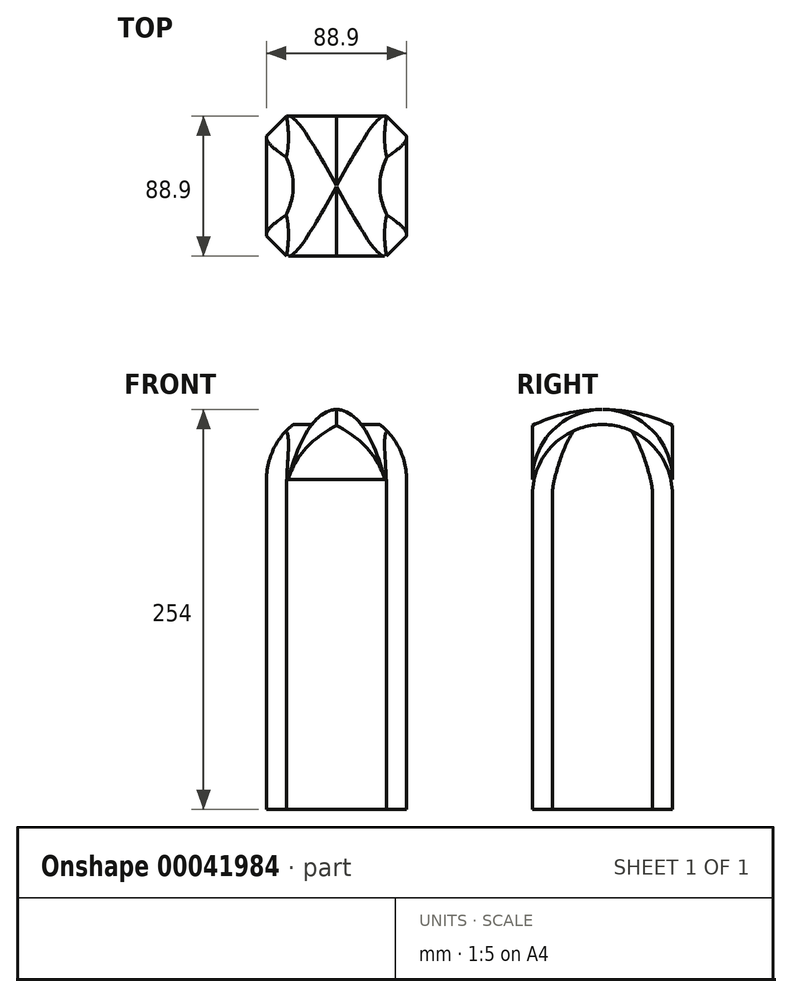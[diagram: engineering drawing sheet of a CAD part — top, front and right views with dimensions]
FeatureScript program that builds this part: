
annotation { "Feature Type Name" : "Feature", "Feature Type Description" : "" }
export const myFeature = defineFeature(function(context is Context, id is Id, definition is map)
    precondition{}
    {
        {
            var Q0;
            Q0=qCreatedBy(makeId("Top.planeOp"),FACE);
            var sketch = newSketch(context, id + "F0", { "sketchPlane" : qUnion([Q0])});
            skLineSegment(sketch, "E0.bottom", {"start": v(-44.45, 44.45) * mm, "end": v(44.45, 44.45) * mm});
            skLineSegment(sketch, "E0.top", {"start": v(-44.45, -44.45) * mm, "end": v(44.45, -44.45) * mm});
            skLineSegment(sketch, "E0.left", {"start": v(-44.45, 44.45) * mm, "end": v(-44.45, -44.45) * mm});
            skLineSegment(sketch, "E0.right", {"start": v(44.45, 44.45) * mm, "end": v(44.45, -44.45) * mm});
            skLineSegment(sketch, "E1", {"start": v(-44.45, 44.45) * mm, "end": v(44.45, -44.45) * mm});
            skLineSegment(sketch, "E2", {"start": v(44.45, 44.45) * mm, "end": v(-44.45, -44.45) * mm});
            skSolve(sketch);
        }
        {
            var Q0;
            Q0=qSketchRegion(id+"F0",true);
            extrude(context, id + "F1", {"entities" : qUnion([Q0]), "depth" : 152.4 * mm});
        }
        {
            var Q0;
            Q0=makeQuery(id+"F1.opExtrude","SWEPT_EDGE",EDGE,{"disambiguationData":[OSD([sQuery(id+"F0.wireOp",EDGE,"E0.top"),sQuery(id+"F0.wireOp",EDGE,"E0.right"),sQuery(id+"F0.wireOp",EDGE,"E1")])]});
            var Q1;
            Q1=makeQuery(id+"F1.opExtrude","SWEPT_EDGE",EDGE,{"disambiguationData":[OSD([sQuery(id+"F0.wireOp",EDGE,"E0.top"),sQuery(id+"F0.wireOp",EDGE,"E0.left"),sQuery(id+"F0.wireOp",EDGE,"E2")])]});
            var Q2;
            Q2=makeQuery(id+"F1.opExtrude","SWEPT_EDGE",EDGE,{"disambiguationData":[OSD([sQuery(id+"F0.wireOp",EDGE,"E0.bottom"),sQuery(id+"F0.wireOp",EDGE,"E0.right"),sQuery(id+"F0.wireOp",EDGE,"E2")])]});
            var Q3;
            Q3=makeQuery(id+"F1.opExtrude","SWEPT_EDGE",EDGE,{"disambiguationData":[OSD([sQuery(id+"F0.wireOp",EDGE,"E0.bottom"),sQuery(id+"F0.wireOp",EDGE,"E0.left"),sQuery(id+"F0.wireOp",EDGE,"E1")])]});
            chamfer(context, id + "F2", {"entities" : qUnion([Q0, Q1, Q2, Q3]), "width" : 12.7 * mm, "tangentPropagation" : true});
        }
        {
            var Q0;
            {var subQ0=sQuery(id+"F0.wireOp",EDGE,"E0.top");var subQ1=sQuery(id+"F0.wireOp",EDGE,"E0.left");Q0=makeQuery(id+"F2.opChamfer","BLEND_EDGE",EDGE,{"blendedFrom":[makeQuery(id+"F1.opExtrude","SWEPT_EDGE",EDGE,{"disambiguationData":[OSD([subQ0,subQ1,sQuery(id+"F0.wireOp",EDGE,"E2")])]}),makeQuery(id+"F1.opExtrude","CAP_FACE",FACE,{"disambiguationData":[OSD([sQuery(id+"F0.wireOp",EDGE,"E0.bottom"),subQ0,subQ1,sQuery(id+"F0.wireOp",EDGE,"E0.right")])],"isStart":false})],"blendedInto":[makeQuery(id+"F1.opExtrude","CAP_FACE",FACE,{"disambiguationData":[OSD([sQuery(id+"F0.wireOp",EDGE,"E0.bottom"),subQ0,subQ1,sQuery(id+"F0.wireOp",EDGE,"E0.right")])],"isStart":false})]});}
            var Q1;
            {var subQ0=sQuery(id+"F0.wireOp",EDGE,"E0.bottom");var subQ1=sQuery(id+"F0.wireOp",EDGE,"E0.left");Q1=makeQuery(id+"F2.opChamfer","BLEND_EDGE",EDGE,{"blendedFrom":[makeQuery(id+"F1.opExtrude","SWEPT_EDGE",EDGE,{"disambiguationData":[OSD([subQ0,subQ1,sQuery(id+"F0.wireOp",EDGE,"E1")])]}),makeQuery(id+"F1.opExtrude","CAP_FACE",FACE,{"disambiguationData":[OSD([subQ0,sQuery(id+"F0.wireOp",EDGE,"E0.top"),subQ1,sQuery(id+"F0.wireOp",EDGE,"E0.right")])],"isStart":false})],"blendedInto":[makeQuery(id+"F1.opExtrude","CAP_FACE",FACE,{"disambiguationData":[OSD([subQ0,sQuery(id+"F0.wireOp",EDGE,"E0.top"),subQ1,sQuery(id+"F0.wireOp",EDGE,"E0.right")])],"isStart":false})]});}
            var Q2;
            {var subQ0=sQuery(id+"F0.wireOp",EDGE,"E0.bottom");var subQ1=sQuery(id+"F0.wireOp",EDGE,"E0.right");Q2=makeQuery(id+"F2.opChamfer","BLEND_EDGE",EDGE,{"blendedFrom":[makeQuery(id+"F1.opExtrude","SWEPT_EDGE",EDGE,{"disambiguationData":[OSD([subQ0,subQ1,sQuery(id+"F0.wireOp",EDGE,"E2")])]}),makeQuery(id+"F1.opExtrude","CAP_FACE",FACE,{"disambiguationData":[OSD([subQ0,sQuery(id+"F0.wireOp",EDGE,"E0.top"),sQuery(id+"F0.wireOp",EDGE,"E0.left"),subQ1])],"isStart":false})],"blendedInto":[makeQuery(id+"F1.opExtrude","CAP_FACE",FACE,{"disambiguationData":[OSD([subQ0,sQuery(id+"F0.wireOp",EDGE,"E0.top"),sQuery(id+"F0.wireOp",EDGE,"E0.left"),subQ1])],"isStart":false})]});}
            var Q3;
            {var subQ0=sQuery(id+"F0.wireOp",EDGE,"E0.top");var subQ1=sQuery(id+"F0.wireOp",EDGE,"E0.right");Q3=makeQuery(id+"F2.opChamfer","BLEND_EDGE",EDGE,{"blendedFrom":[makeQuery(id+"F1.opExtrude","SWEPT_EDGE",EDGE,{"disambiguationData":[OSD([subQ0,subQ1,sQuery(id+"F0.wireOp",EDGE,"E1")])]}),makeQuery(id+"F1.opExtrude","CAP_FACE",FACE,{"disambiguationData":[OSD([sQuery(id+"F0.wireOp",EDGE,"E0.bottom"),subQ0,sQuery(id+"F0.wireOp",EDGE,"E0.left"),subQ1])],"isStart":false})],"blendedInto":[makeQuery(id+"F1.opExtrude","CAP_FACE",FACE,{"disambiguationData":[OSD([sQuery(id+"F0.wireOp",EDGE,"E0.bottom"),subQ0,sQuery(id+"F0.wireOp",EDGE,"E0.left"),subQ1])],"isStart":false})]});}
            fillet(context, id + "F3", {"entities" : qUnion([Q0, Q1, Q2, Q3]), "radius" : 53.97 * mm, "tangentPropagation" : true, "allowEdgeOverflow" : false});
        }
        {
            var Q0;
            Q0=makeQuery(id+"F1.opExtrude","SWEPT_FACE",FACE,{"disambiguationData":[OSD([sQuery(id+"F0.wireOp",EDGE,"E0.left")])]});
            var sketch = newSketch(context, id + "F4", { "sketchPlane" : qUnion([Q0])});
            skLineSegment(sketch, "E3.0", {"start": v(-44.45, 98.43) * mm, "end": v(-44.45, 142.24) * mm});
            skLineSegment(sketch, "E4.0", {"start": v(44.45, 142.24) * mm, "end": v(44.45, 98.43) * mm});
            skArc(sketch, "E5", {"start": v(44.45, 98.43) * mm, "mid": v(0, 142.88) * mm, "end": v(-44.45, 98.43) * mm});
            skFitSpline(sketch, "E6.0", {"points": [v(76.46, 98.43) * mm, v(1000, 76.46) * mm, v(206.38, 333.33) * mm, v(-76.2, 206.38) * mm, v(333.33, -76.2) * mm, v(98.43, 1000) * mm, v(-76.2, -9.52) * mm]});
            skFitSpline(sketch, "E7.0", {"points": [v(-76.46, 98.43) * mm, v(1000, -76.46) * mm, v(-9.52, 333.33) * mm, v(76.2, -9.52) * mm, v(333.33, 76.2) * mm, v(98.43, 1000) * mm, v(76.2, 206.38) * mm]});
            skArc(sketch, "E8", {"start": v(44.45, 107.95) * mm, "mid": v(0, 152.4) * mm, "end": v(-44.45, 107.95) * mm});
            skSolve(sketch);
        }
        {
            var Q0;
            {var subQ1=sQuery(id+"F4.wireOp",EDGE,"E7.0");var subQ3=sQuery(id+"F4.wireOp",EDGE,"E4.0");var subQ5=makeQuery(id+"F4.imprint","INTERSECT",VERTEX,{"derivedFrom":[subQ3,subQ1]});Q0=makeQuery(id+"F4.imprint","IMPRINT",FACE,{"disambiguationData":[TD([[makeQuery(id+"F4.imprint","IMPRINT",EDGE,{"disambiguationData":[TD([[subQ5,-1.0]])],"derivedFrom":subQ3}),-1.0]])]});}
            var Q1;
            {var subQ1=sQuery(id+"F4.wireOp",EDGE,"E6.0");var subQ3=sQuery(id+"F4.wireOp",EDGE,"E3.0");var subQ5=makeQuery(id+"F4.imprint","INTERSECT",VERTEX,{"derivedFrom":[subQ3,subQ1]});Q1=makeQuery(id+"F4.imprint","IMPRINT",FACE,{"disambiguationData":[TD([[makeQuery(id+"F4.imprint","IMPRINT",EDGE,{"disambiguationData":[TD([[subQ5,1.0]])],"derivedFrom":subQ3}),-1.0]])]});}
            extrude(context, id + "F5", {"entities" : qUnion([Q0, Q1]), "operationType" : NewBodyOperationType.REMOVE, "endBound" : BoundingType.THROUGH_ALL, "oppositeDirection" : true, "depth" : 25.4 * mm});
        }
        {
            var Q0;
            Q0=makeQuery(id+"F1.opExtrude","SWEPT_FACE",FACE,{"disambiguationData":[OSD([sQuery(id+"F0.wireOp",EDGE,"E0.top")])]});
            var sketch = newSketch(context, id + "F6", { "sketchPlane" : qUnion([Q0])});
            skLineSegment(sketch, "E9.0", {"start": v(-44.45, 142.24) * mm, "end": v(-44.45, 98.43) * mm});
            skLineSegment(sketch, "E10.0", {"start": v(44.45, 98.43) * mm, "end": v(44.45, 142.24) * mm});
            skFitSpline(sketch, "E11.0", {"points": [v(-76.2, 98.43) * mm, v(1000, -76.2) * mm, v(206.38, 333.33) * mm, v(76.46, 206.38) * mm, v(333.33, 76.46) * mm, v(98.43, 1000) * mm, v(76.46, -9.52) * mm]});
            skFitSpline(sketch, "E12.0", {"points": [v(76.2, 98.43) * mm, v(1000, 76.2) * mm, v(-9.52, 333.33) * mm, v(-76.46, -9.52) * mm, v(333.33, -76.46) * mm, v(98.43, 1000) * mm, v(-76.46, 206.38) * mm]});
            skArc(sketch, "E13", {"start": v(44.45, 98.43) * mm, "mid": v(0, 142.88) * mm, "end": v(-44.45, 98.42) * mm, "construction": true});
            skLineSegment(sketch, "E14.0.0", {"start": v(0, 152.4) * mm, "end": v(0, 152.4) * mm});
            skLineSegment(sketch, "E14.0.4", {"start": v(44.45, 142.24) * mm, "end": v(44.45, 98.43) * mm});
            skEllipticalArc(sketch, "E14.0.5", {});
            skArc(sketch, "E15", {"start": v(44.45, 107.95) * mm, "mid": v(0, 152.4) * mm, "end": v(-44.45, 107.95) * mm});
            skEllipticalArc(sketch, "E16.0.3", {});
            skLineSegment(sketch, "E16.0.4", {"start": v(-44.45, 98.43) * mm, "end": v(-44.45, 142.24) * mm});
            const initialGuessF6  = {"E14.0.5": [-0.00013217702908781167, 0.098425, 1, 0, 0.0763321770290878, 0.053975, 0.9470811641255592, 1.5690647228987853], "E16.0.3": [0.00013217702908779883, 0.098425, -1, 0, 0.0763321770290878, 0.053975, 4.714120584280801, 5.336104143054027]};
            skSetInitialGuess(sketch, initialGuessF6);
            skSolve(sketch);
        }
        {
            var Q0;
            Q0=qSketchRegion(id+"F6",true);
            extrude(context, id + "F7", {"entities" : qUnion([Q0]), "operationType" : NewBodyOperationType.REMOVE, "endBound" : BoundingType.THROUGH_ALL, "oppositeDirection" : true, "depth" : 25.4 * mm});
        }
        {
            var Q0;
            Q0=makeQuery(id+"F1.opExtrude","CAP_FACE",FACE,{"disambiguationData":[OSD([sQuery(id+"F0.wireOp",EDGE,"E0.bottom"),sQuery(id+"F0.wireOp",EDGE,"E0.top"),sQuery(id+"F0.wireOp",EDGE,"E0.left"),sQuery(id+"F0.wireOp",EDGE,"E0.right")])],"isStart":true});
            extrude(context, id + "F8", {"entities" : qUnion([Q0]), "operationType" : NewBodyOperationType.ADD, "depth" : 101.6 * mm});
        }
    });
